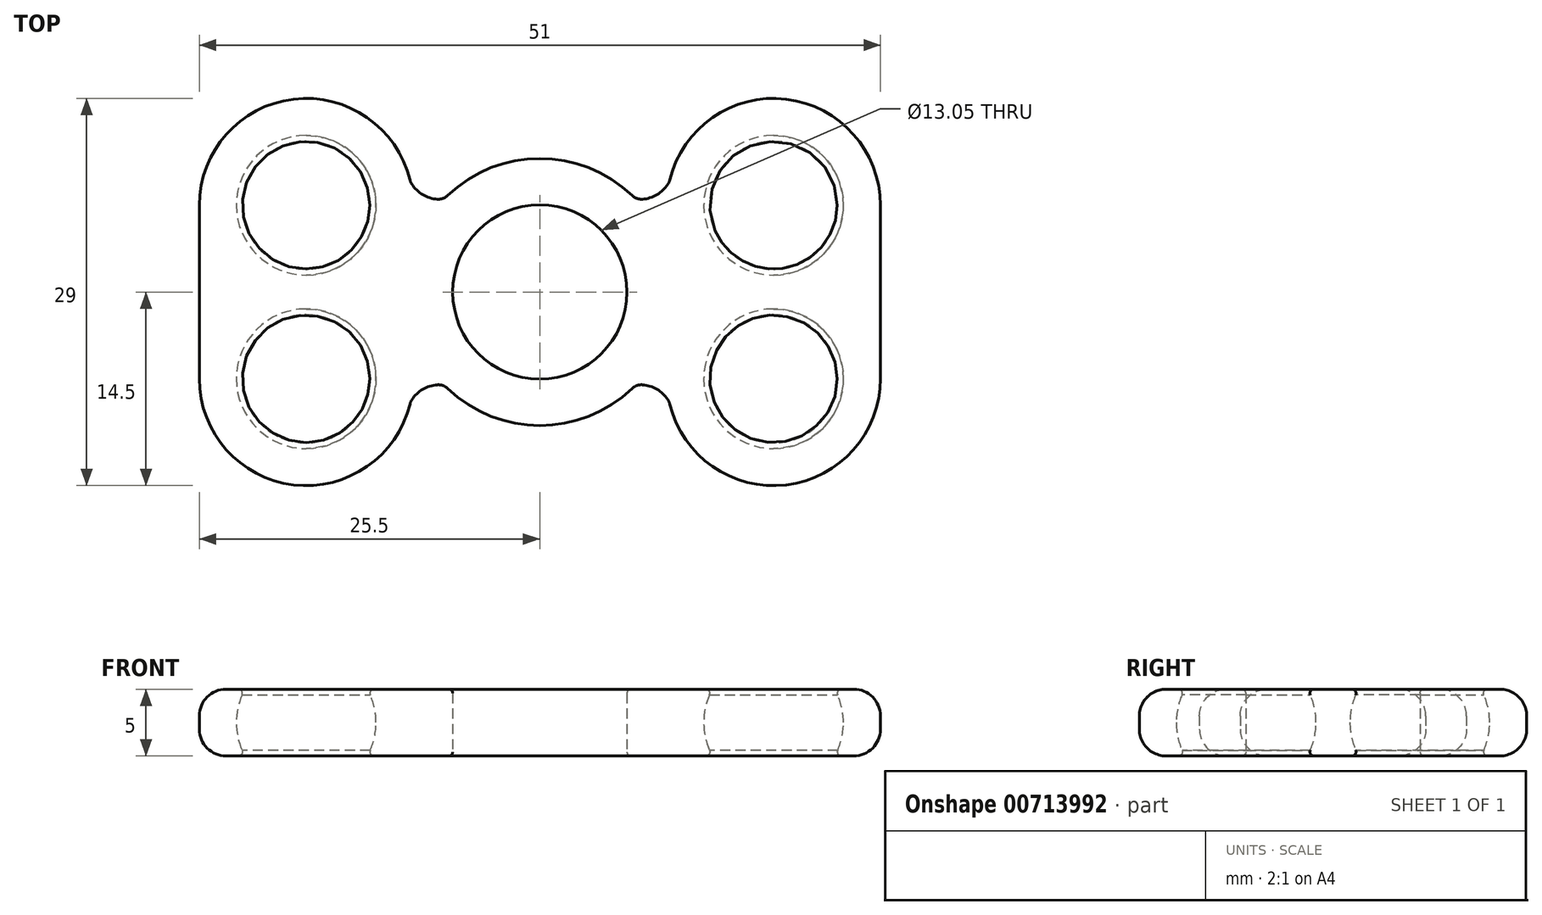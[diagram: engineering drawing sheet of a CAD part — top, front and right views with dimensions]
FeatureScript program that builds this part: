
annotation { "Feature Type Name" : "Feature", "Feature Type Description" : "" }
export const myFeature = defineFeature(function(context is Context, id is Id, definition is map)
    precondition{}
    {
        {
            var Q0;
            Q0=qCreatedBy(makeId("Top.planeOp"),FACE);
            var sketch = newSketch(context, id + "F0", { "sketchPlane" : qUnion([Q0])});
            skCircle(sketch, "E0", {"center": v(0, 0) * mm, "radius": 6.53 * mm});
            skArc(sketch, "E1", {"start": v(6.91, 7.23) * mm, "mid": v(0, 10) * mm, "end": v(-6.91, 7.23) * mm});
            skCircle(sketch, "E2", {"center": v(17.5, 6.5) * mm, "radius": 2.5 * mm});
            skCircle(sketch, "E3", {"center": v(17.5, -6.5) * mm, "radius": 2.5 * mm});
            skArc(sketch, "E4", {"start": v(9.73, -8.38) * mm, "mid": v(18.45, -14.44) * mm, "end": v(25.5, -6.5) * mm});
            skLineSegment(sketch, "E5", {"start": v(25.5, 6.5) * mm, "end": v(25.5, -6.5) * mm});
            skArc(sketch, "E6", {"start": v(7.68, 6.95) * mm, "mid": v(8.76, 7.29) * mm, "end": v(9.59, 8.07) * mm});
            skArc(sketch, "E7", {"start": v(9.59, -8.07) * mm, "mid": v(8.76, -7.29) * mm, "end": v(7.68, -6.95) * mm});
            skArc(sketch, "E8.trimOffspring", {"start": v(25.5, 6.5) * mm, "mid": v(18.45, 14.44) * mm, "end": v(9.73, 8.38) * mm});
            skLineSegment(sketch, "E9", {"start": v(0, 15.27) * mm, "end": v(0, -14.8) * mm});
            skPoint(sketch, "E10.visualSharp", {"position": v(7.18, 6.96) * mm});
            skArc(sketch, "E10.filletArc", {"start": v(6.91, 7.23) * mm, "mid": v(7.27, 7) * mm, "end": v(7.68, 6.95) * mm});
            skPoint(sketch, "E11.visualSharp", {"position": v(9.7, 8.24) * mm});
            skArc(sketch, "E11.filletArc", {"start": v(9.59, 8.07) * mm, "mid": v(9.67, 8.22) * mm, "end": v(9.73, 8.38) * mm});
            skPoint(sketch, "E12.visualSharp", {"position": v(7.18, -6.96) * mm});
            skArc(sketch, "E12.filletArc", {"start": v(7.68, -6.95) * mm, "mid": v(7.27, -7) * mm, "end": v(6.91, -7.23) * mm});
            skPoint(sketch, "E13.visualSharp", {"position": v(9.7, -8.24) * mm});
            skArc(sketch, "E13.filletArc", {"start": v(9.73, -8.38) * mm, "mid": v(9.67, -8.22) * mm, "end": v(9.59, -8.07) * mm});
            skArc(sketch, "E14.MirrorCS", {"start": v(-9.73, -8.38) * mm, "mid": v(-9.67, -8.22) * mm, "end": v(-9.59, -8.07) * mm});
            skArc(sketch, "E15.MirrorCS", {"start": v(-7.68, 6.95) * mm, "mid": v(-8.76, 7.29) * mm, "end": v(-9.59, 8.07) * mm});
            skArc(sketch, "E16.MirrorCS", {"start": v(-6.91, 7.23) * mm, "mid": v(-7.27, 7) * mm, "end": v(-7.68, 6.95) * mm});
            skArc(sketch, "E17.MirrorCS", {"start": v(-9.59, 8.07) * mm, "mid": v(-9.67, 8.22) * mm, "end": v(-9.73, 8.38) * mm});
            skArc(sketch, "E18.MirrorCS", {"start": v(-7.68, -6.95) * mm, "mid": v(-7.27, -7) * mm, "end": v(-6.91, -7.23) * mm});
            skArc(sketch, "E19.MirrorCS", {"start": v(-9.59, -8.07) * mm, "mid": v(-8.76, -7.29) * mm, "end": v(-7.68, -6.95) * mm});
            skPoint(sketch, "E20.MirrorP", {"position": v(-9.7, 8.24) * mm});
            skPoint(sketch, "E21.MirrorP", {"position": v(-7.18, -6.96) * mm});
            skCircle(sketch, "E22.MirrorC", {"center": v(-17.5, -6.5) * mm, "radius": 2.5 * mm});
            skArc(sketch, "E23.MirrorCS", {"start": v(-25.5, 6.5) * mm, "mid": v(-18.45, 14.44) * mm, "end": v(-9.73, 8.38) * mm});
            skLineSegment(sketch, "E24.MirrorCS", {"start": v(-25.5, 6.5) * mm, "end": v(-25.5, -6.5) * mm});
            skPoint(sketch, "E25.MirrorP", {"position": v(-9.7, -8.24) * mm});
            skArc(sketch, "E26.MirrorCS", {"start": v(-9.73, -8.38) * mm, "mid": v(-18.45, -14.44) * mm, "end": v(-25.5, -6.5) * mm});
            skCircle(sketch, "E27.MirrorC", {"center": v(-17.5, 6.5) * mm, "radius": 2.5 * mm});
            skPoint(sketch, "E28.MirrorP", {"position": v(-7.18, 6.96) * mm});
            skArc(sketch, "E29.trimOffspring", {"start": v(-6.91, -7.23) * mm, "mid": v(0, -10) * mm, "end": v(6.91, -7.23) * mm});
            skSolve(sketch);
        }
        {
            var Q0;
            Q0 = qSketchRegion(id + "F0", true);
            extrude(context, id + "F1", {"entities" : qUnion([Q0]), "depth" : 2.5 * mm, "offsetDistance" : 25 * mm});
        }
        {
            var Q0;
            Q0 = qSketchRegion(id + "F0", true);
            extrude(context, id + "F2", {"entities" : qUnion([Q0]), "operationType" : NewBodyOperationType.ADD, "oppositeDirection" : true, "depth" : 2.5 * mm, "offsetDistance" : 25 * mm});
        }
        {
            var Q0;
            Q0=qCreatedBy(makeId("Top.planeOp"),FACE);
            var sketch = newSketch(context, id + "F3", { "sketchPlane" : qUnion([Q0])});
            skArc(sketch, "E30", {"start": v(-17.5, 11.73) * mm, "mid": v(-22.73, 6.5) * mm, "end": v(-17.5, 1.27) * mm});
            skLineSegment(sketch, "E31", {"start": v(-17.5, 11.73) * mm, "end": v(-17.5, 1.27) * mm});
            skSolve(sketch);
        }
        {
            var Q0;
            Q0 = qSketchRegion(id + "F3", true);
            var Q1;
            Q1=sQuery(id+"F3.wireOp",EDGE,"E31");
            revolve(context, id + "F4", {"operationType" : NewBodyOperationType.REMOVE, "surfaceOperationType" : NewSurfaceOperationType.NEW, "entities" : qUnion([Q0]), "axis" : qUnion([Q1]), "revolveType" : RevolveType.FULL, "oppositeDirection" : true});
        }
        {
            var Q0;
            Q0=qCreatedBy(makeId("Top.planeOp"),FACE);
            var sketch = newSketch(context, id + "F5", { "sketchPlane" : qUnion([Q0])});
            skArc(sketch, "E32", {"start": v(-17.5, -1.27) * mm, "mid": v(-22.73, -6.5) * mm, "end": v(-17.5, -11.73) * mm});
            skLineSegment(sketch, "E33", {"start": v(-17.5, -1.27) * mm, "end": v(-17.5, -11.73) * mm});
            skSolve(sketch);
        }
        {
            var Q0;
            Q0=makeQuery(id+"F5.imprint","IMPRINT",FACE,{"disambiguationData":[TD([[makeQuery(id+"F5.imprint","IMPRINT",EDGE,{"derivedFrom":sQuery(id+"F5.wireOp",EDGE,"E32")}),1.0]])]});
            var Q1;
            Q1=sQuery(id+"F5.wireOp",EDGE,"E33");
            revolve(context, id + "F6", {"operationType" : NewBodyOperationType.REMOVE, "surfaceOperationType" : NewSurfaceOperationType.NEW, "entities" : qUnion([Q0]), "axis" : qUnion([Q1]), "revolveType" : RevolveType.FULL, "oppositeDirection" : true});
        }
        {
            var Q0;
            Q0=qCreatedBy(makeId("Top.planeOp"),FACE);
            var sketch = newSketch(context, id + "F7", { "sketchPlane" : qUnion([Q0])});
            skArc(sketch, "E34", {"start": v(17.5, 11.73) * mm, "mid": v(12.27, 6.5) * mm, "end": v(17.5, 1.27) * mm});
            skLineSegment(sketch, "E35", {"start": v(17.5, 11.73) * mm, "end": v(17.5, 1.27) * mm});
            skSolve(sketch);
        }
        {
            var Q0;
            Q0=makeQuery(id+"F7.imprint","IMPRINT",FACE,{"disambiguationData":[TD([[makeQuery(id+"F7.imprint","IMPRINT",EDGE,{"derivedFrom":sQuery(id+"F7.wireOp",EDGE,"E34")}),1.0]])]});
            var Q1;
            Q1=sQuery(id+"F7.wireOp",EDGE,"E35");
            revolve(context, id + "F8", {"operationType" : NewBodyOperationType.REMOVE, "surfaceOperationType" : NewSurfaceOperationType.NEW, "entities" : qUnion([Q0]), "axis" : qUnion([Q1]), "revolveType" : RevolveType.FULL, "oppositeDirection" : true});
        }
        {
            var Q0;
            Q0=qCreatedBy(makeId("Top.planeOp"),FACE);
            var sketch = newSketch(context, id + "F9", { "sketchPlane" : qUnion([Q0])});
            skArc(sketch, "E36", {"start": v(17.5, -1.27) * mm, "mid": v(12.27, -6.5) * mm, "end": v(17.5, -11.73) * mm});
            skLineSegment(sketch, "E37", {"start": v(17.5, -1.27) * mm, "end": v(17.5, -11.73) * mm});
            skSolve(sketch);
        }
        {
            var Q0;
            Q0=makeQuery(id+"F9.imprint","IMPRINT",FACE,{"disambiguationData":[TD([[makeQuery(id+"F9.imprint","IMPRINT",EDGE,{"derivedFrom":sQuery(id+"F9.wireOp",EDGE,"E36")}),1.0]])]});
            var Q1;
            Q1=sQuery(id+"F9.wireOp",EDGE,"E37");
            revolve(context, id + "F10", {"operationType" : NewBodyOperationType.REMOVE, "surfaceOperationType" : NewSurfaceOperationType.NEW, "entities" : qUnion([Q0]), "axis" : qUnion([Q1]), "revolveType" : RevolveType.FULL, "oppositeDirection" : true});
        }
        {
            var Q0;
            Q0=makeQuery(id+"F2.opExtrude","CAP_EDGE",EDGE,{"disambiguationData":[OSD([sQuery(id+"F0.wireOp",EDGE,"E1")])],"isStart":false});
            var Q1;
            Q1=makeQuery(id+"F1.opExtrude","CAP_EDGE",EDGE,{"disambiguationData":[OSD([sQuery(id+"F0.wireOp",EDGE,"E1")])],"isStart":false});
            fillet(context, id + "F11", {"entities" : qUnion([Q0, Q1]), "radius" : 2 * mm, "tangentPropagation" : true, "allowEdgeOverflow" : false});
        }
        {
            var Q0;
            Q0=makeQuery(id+"F4.boolean.opBoolean","COPY",FACE,{"derivedFrom":makeQuery(id+"F4.opRevolve","SWEPT_FACE",FACE,{"disambiguationData":[OSD([sQuery(id+"F3.wireOp",EDGE,"E30")])]})});
            var Q1;
            Q1=makeQuery(id+"F6.boolean.opBoolean","COPY",FACE,{"derivedFrom":makeQuery(id+"F6.opRevolve","SWEPT_FACE",FACE,{"disambiguationData":[OSD([sQuery(id+"F5.wireOp",EDGE,"E32")])]})});
            var Q2;
            {var subQ0=sQuery(id+"F0.wireOp",EDGE,"E0");Q2=makeQuery(id+"F2.boolean.opBoolean","MERGE",FACE,{"derivedFrom":[makeQuery(id+"F1.opExtrude","SWEPT_FACE",FACE,{"disambiguationData":[OSD([subQ0])]}),makeQuery(id+"F2.opExtrude","SWEPT_FACE",FACE,{"disambiguationData":[OSD([subQ0])]})]});}
            var Q3;
            Q3=makeQuery(id+"F8.boolean.opBoolean","COPY",FACE,{"derivedFrom":makeQuery(id+"F8.opRevolve","SWEPT_FACE",FACE,{"disambiguationData":[OSD([sQuery(id+"F7.wireOp",EDGE,"E34")])]})});
            var Q4;
            Q4=makeQuery(id+"F10.boolean.opBoolean","COPY",FACE,{"derivedFrom":makeQuery(id+"F10.opRevolve","SWEPT_FACE",FACE,{"disambiguationData":[OSD([sQuery(id+"F9.wireOp",EDGE,"E36")])]})});
            fillet(context, id + "F12", {"entities" : qUnion([Q0, Q1, Q2, Q3, Q4]), "radius" : .3 * mm, "tangentPropagation" : true, "allowEdgeOverflow" : false});
        }
    });
